# Revit family: FU_Chair_Sandler_4400-TSNF_A
name_source: partatom
category: Furniture
units: mm (PartAtom-declared; Revit-internal decimal feet)

## family parameters
Always vertical = Yes
Cut with Voids When Loaded = No
OmniClass Number = 23.40.20.00
OmniClass Title = General Furniture and Specialties
Room Calculation Point = No
Shared = No
Work Plane-Based = No

## types (1)
- 4400TSNF-A
    Default Elevation = 0 mm  [stored 0 ft]
    Depth = 560 mm  [stored 1.83727 ft]
    Description = Folding chair. Double rolled steel frame with tip up seat. ‘A’ shape back. Upholstered seat and back. Includes integral linking device. *** Please note that there is an MOQ of 201 pieces for this model in Silver and Bronze. There is no MOQ on Black frames.***
    Frame = Metal - Steel - Bronze
    Height = 860 mm
    Manufacturer = Sandler
    Model = 4400TSNF-A
    Rubber = Rubber, Black
    URL = https://www.sandlerseating.com
    Upholstery = Fabric - Mainline Flax - Embankment MLF50
    Width = 460 mm  [stored 1.50919 ft]

note: [stored X ft] marks values corroborated as IEEE doubles in the binary element streams (Revit-internal decimal feet)

## geometry (parser evidence)
native form markers: Sweep x12
no freeform markers — native parametric forms only
